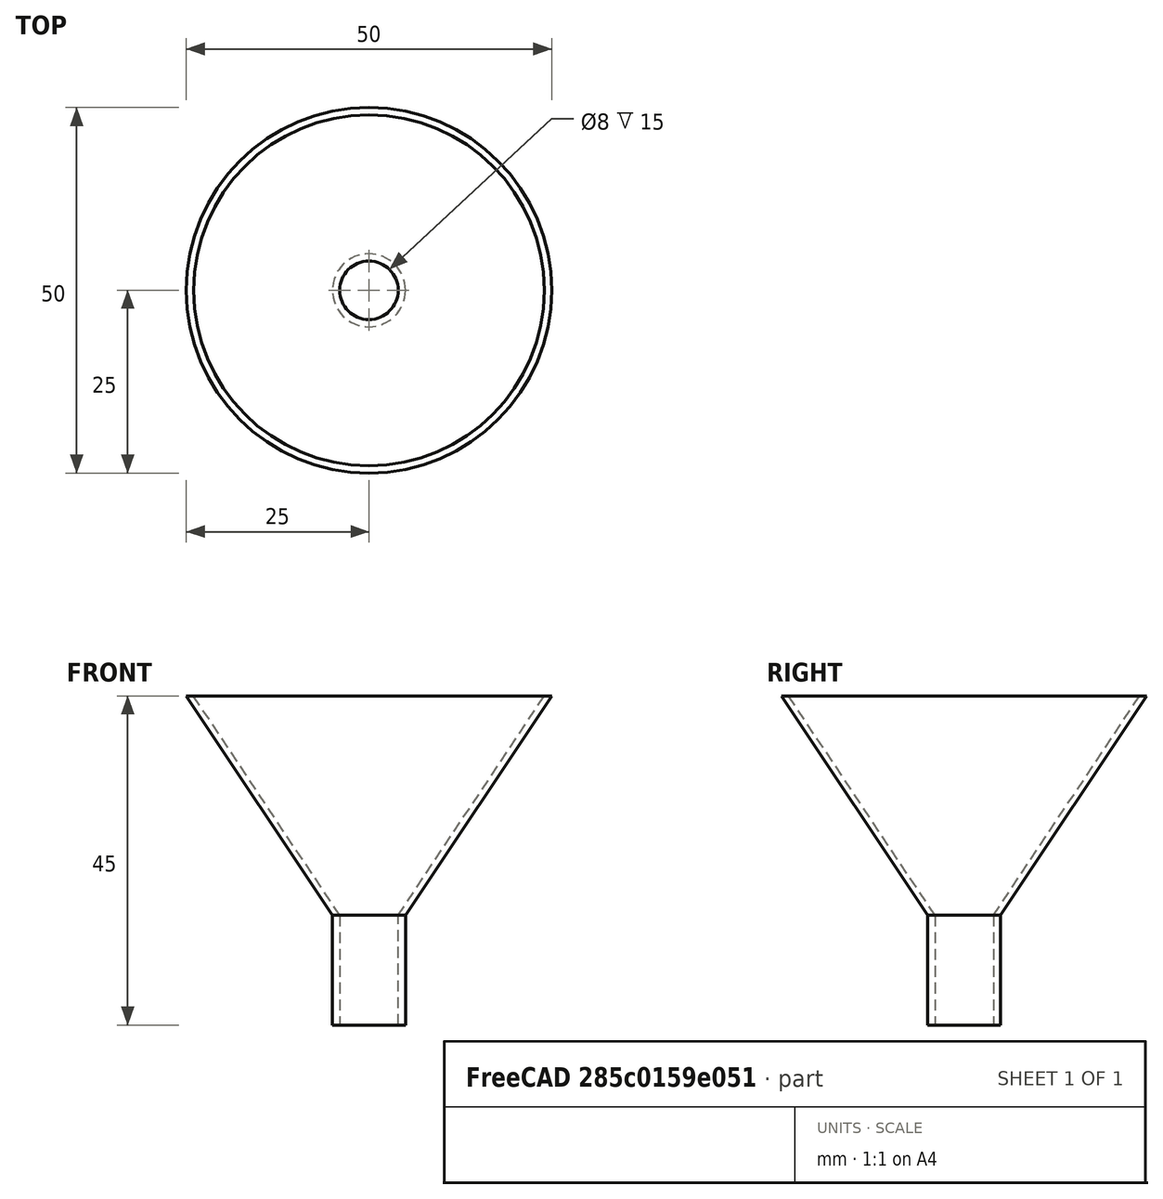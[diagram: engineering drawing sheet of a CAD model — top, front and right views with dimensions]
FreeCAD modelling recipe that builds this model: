
FCSTD DOCUMENT  (FreeCAD 0.21R33694 (Git))
Label: OJT1_T14R03.envut
License: All rights reserved
LicenseURL: http://en.wikipedia.org/wiki/All_rights_reserved
objects: Part::Cylinder×2, Part::Cut×2, Part::Cone×2, Part::Fuse×1
note: 7 computed .brp shape members not serialized (recipe doc carries the construction recipe); baked Part::Feature solids carry a one-line shape summary decoded from their .brp

FEATURE [Part::Cylinder] Cylinder  label="Cilindre"
  Angle = 360
  AttacherType = Attacher::AttachEngine3D
  FirstAngle = 0
  Height = 15
  Radius = 5
  SecondAngle = 0
FEATURE [Part::Cylinder] Cylinder001  label="Cilindre001"
  Angle = 360
  AttacherType = Attacher::AttachEngine3D
  FirstAngle = 0
  Height = 15
  Radius = 4
  SecondAngle = 0
FEATURE [Part::Cut] Cut
  Base = -> Cylinder
  Refine = true
  Tool = -> Cylinder001
FEATURE [Part::Cone] Cone  label="Con"
  Angle = 360
  AttacherType = Attacher::AttachEngine3D
  Height = 30
  Radius1 = 5
  Radius2 = 25
FEATURE [Part::Cone] Cone001  label="Con001"
  Angle = 360
  AttacherType = Attacher::AttachEngine3D
  Height = 30
  Radius1 = 4
  Radius2 = 24
FEATURE [Part::Cut] Cut001
  Base = -> Cone
  Placement = pos=(0,0,15) rot=(0,0,1;0rad)
  Refine = true
  Tool = -> Cone001
FEATURE [Part::Fuse] Fusion
  Base = -> Cut
  Refine = true
  Tool = -> Cut001
